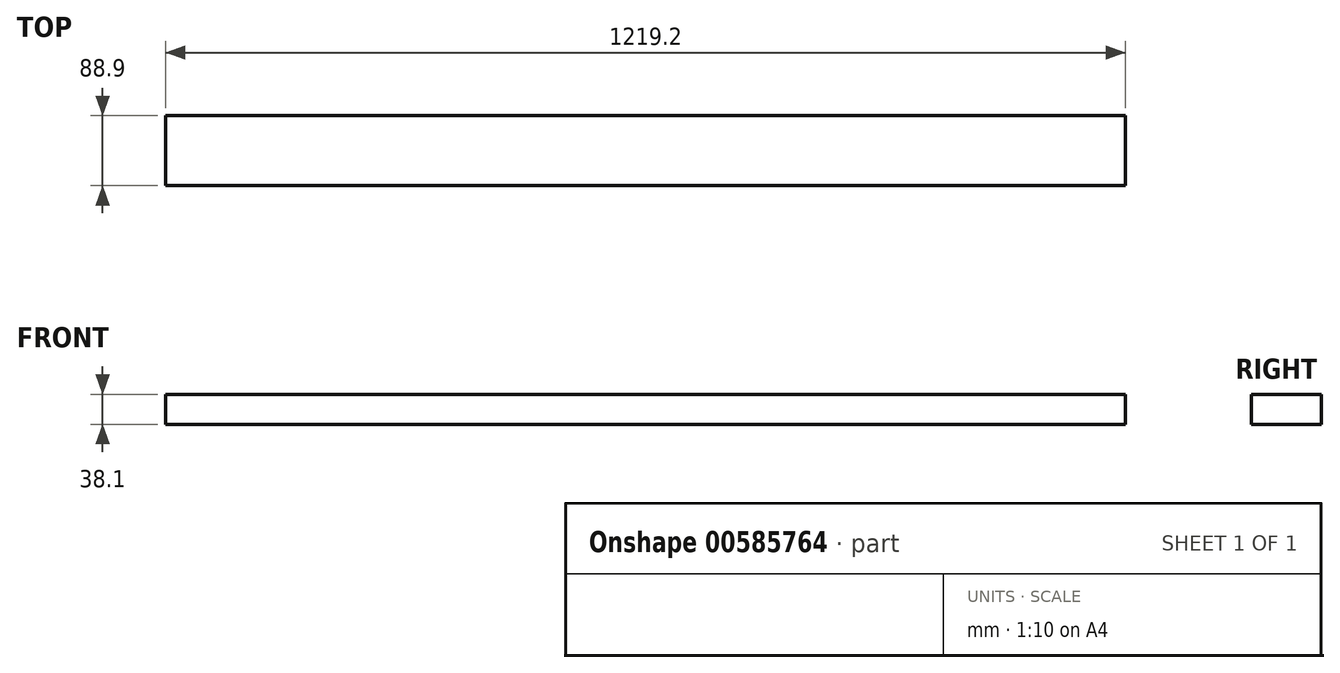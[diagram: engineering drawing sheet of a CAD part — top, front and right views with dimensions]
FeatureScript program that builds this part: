
annotation { "Feature Type Name" : "Feature", "Feature Type Description" : "" }
export const myFeature = defineFeature(function(context is Context, id is Id, definition is map)
    precondition{}
    {
        {
            var Q0;
            Q0=qCreatedBy(makeId("Front.planeOp"),FACE);
            var sketch = newSketch(context, id + "F0", { "sketchPlane" : qUnion([Q0])});
            skLineSegment(sketch, "E0", {"start": v(0, 0) * mm, "end": v(-1219.2, 0) * mm});
            skLineSegment(sketch, "E1", {"start": v(-1219.2, 0) * mm, "end": v(-1219.2, 38.1) * mm});
            skLineSegment(sketch, "E2", {"start": v(-1219.2, 38.1) * mm, "end": v(0, 38.1) * mm});
            skLineSegment(sketch, "E3", {"start": v(0, 38.1) * mm, "end": v(0, 0) * mm});
            skSolve(sketch);
        }
        {
            var Q0;
            Q0=qSketchRegion(id+"F0",true);
            extrude(context, id + "F1", {"entities" : qUnion([Q0]), "depth" : 88.9 * mm, "offsetDistance" : 25.4 * mm});
        }
    });
